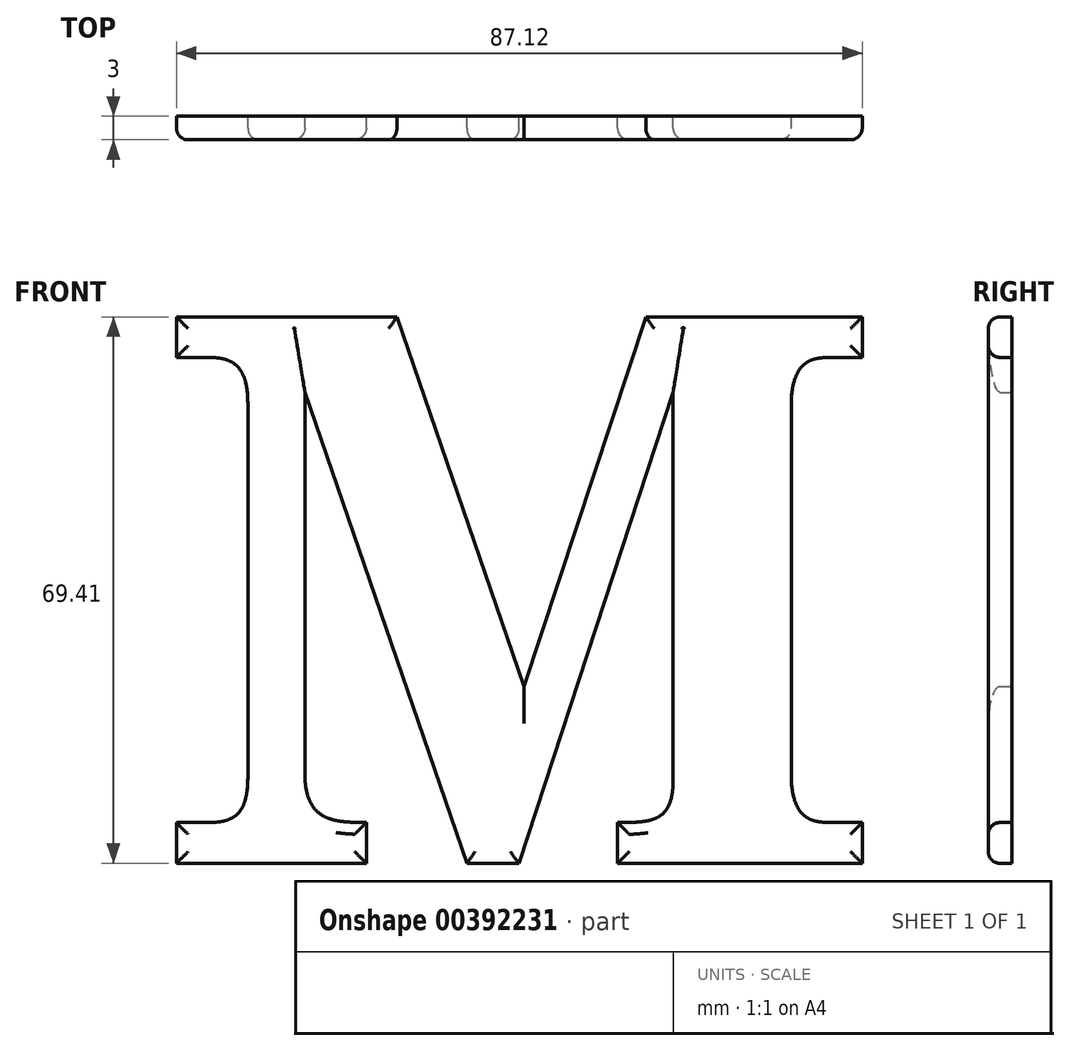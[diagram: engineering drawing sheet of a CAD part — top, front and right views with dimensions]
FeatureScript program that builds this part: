
annotation { "Feature Type Name" : "Feature", "Feature Type Description" : "" }
export const myFeature = defineFeature(function(context is Context, id is Id, definition is map)
    precondition{}
    {
        {
            var Q0;
            Q0=qCreatedBy(makeId("Front.planeOp"),FACE);
            var sketch = newSketch(context, id + "F0", { "sketchPlane" : qUnion([Q0])});
            skText(sketch, "E0", { "text": "M", "fontName": "NotoSerif-Bold.ttf"});
            const initialGuessF0  = {"E0": [0, 0, 1, 0, 0.07]};
            skSetInitialGuess(sketch, initialGuessF0);
            skSolve(sketch);
        }
        {
            var Q0;
            Q0 = qSketchRegion(id + "F0", true);
            extrude(context, id + "F1", {"entities" : qUnion([Q0]), "depth" : 3 * mm});
        }
        {
            var Q0;
            Q0=makeQuery(id+"F1.opExtrude","CAP_FACE",FACE,{"disambiguationData":[OSD([sQuery(id+"F0.wireOp",EDGE,"E0.sketch_text.stroke-0"),sQuery(id+"F0.wireOp",EDGE,"E0.sketch_text.stroke-1"),sQuery(id+"F0.wireOp",EDGE,"E0.sketch_text.stroke-2"),sQuery(id+"F0.wireOp",EDGE,"E0.sketch_text.stroke-3"),sQuery(id+"F0.wireOp",EDGE,"E0.sketch_text.stroke-4"),sQuery(id+"F0.wireOp",EDGE,"E0.sketch_text.stroke-5"),sQuery(id+"F0.wireOp",EDGE,"E0.sketch_text.stroke-6"),sQuery(id+"F0.wireOp",EDGE,"E0.sketch_text.stroke-7"),sQuery(id+"F0.wireOp",EDGE,"E0.sketch_text.stroke-8"),sQuery(id+"F0.wireOp",EDGE,"E0.sketch_text.stroke-9"),sQuery(id+"F0.wireOp",EDGE,"E0.sketch_text.stroke-10"),sQuery(id+"F0.wireOp",EDGE,"E0.sketch_text.stroke-11"),sQuery(id+"F0.wireOp",EDGE,"E0.sketch_text.stroke-12"),sQuery(id+"F0.wireOp",EDGE,"E0.sketch_text.stroke-13"),sQuery(id+"F0.wireOp",EDGE,"E0.sketch_text.stroke-14"),sQuery(id+"F0.wireOp",EDGE,"E0.sketch_text.stroke-15"),sQuery(id+"F0.wireOp",EDGE,"E0.sketch_text.stroke-16"),sQuery(id+"F0.wireOp",EDGE,"E0.sketch_text.stroke-17"),sQuery(id+"F0.wireOp",EDGE,"E0.sketch_text.stroke-18"),sQuery(id+"F0.wireOp",EDGE,"E0.sketch_text.stroke-19"),sQuery(id+"F0.wireOp",EDGE,"E0.sketch_text.stroke-20"),sQuery(id+"F0.wireOp",EDGE,"E0.sketch_text.stroke-21"),sQuery(id+"F0.wireOp",EDGE,"E0.sketch_text.stroke-22"),sQuery(id+"F0.wireOp",EDGE,"E0.sketch_text.stroke-23"),sQuery(id+"F0.wireOp",EDGE,"E0.sketch_text.stroke-24"),sQuery(id+"F0.wireOp",EDGE,"E0.sketch_text.stroke-25"),sQuery(id+"F0.wireOp",EDGE,"E0.sketch_text.stroke-26"),sQuery(id+"F0.wireOp",EDGE,"E0.sketch_text.stroke-27"),sQuery(id+"F0.wireOp",EDGE,"E0.sketch_text.stroke-28"),sQuery(id+"F0.wireOp",EDGE,"E0.sketch_text.stroke-29"),sQuery(id+"F0.wireOp",EDGE,"E0.sketch_text.stroke-30"),sQuery(id+"F0.wireOp",EDGE,"E0.sketch_text.stroke-31"),sQuery(id+"F0.wireOp",EDGE,"E0.sketch_text.stroke-32"),sQuery(id+"F0.wireOp",EDGE,"E0.sketch_text.stroke-33"),sQuery(id+"F0.wireOp",EDGE,"E0.sketch_text.stroke-34"),sQuery(id+"F0.wireOp",EDGE,"E0.sketch_text.stroke-35"),sQuery(id+"F0.wireOp",EDGE,"E0.sketch_text.stroke-36"),sQuery(id+"F0.wireOp",EDGE,"E0.sketch_text.stroke-37"),sQuery(id+"F0.wireOp",EDGE,"E0.sketch_text.stroke-38"),sQuery(id+"F0.wireOp",EDGE,"E0.sketch_text.stroke-39"),sQuery(id+"F0.wireOp",EDGE,"E0.sketch_text.stroke-40"),sQuery(id+"F0.wireOp",EDGE,"E0.sketch_text.stroke-41"),sQuery(id+"F0.wireOp",EDGE,"E0.sketch_text.stroke-42"),sQuery(id+"F0.wireOp",EDGE,"E0.sketch_text.stroke-43"),sQuery(id+"F0.wireOp",EDGE,"E0.sketch_text.stroke-44"),sQuery(id+"F0.wireOp",EDGE,"E0.sketch_text.stroke-45"),sQuery(id+"F0.wireOp",EDGE,"E0.sketch_text.stroke-46"),sQuery(id+"F0.wireOp",EDGE,"E0.sketch_text.stroke-47"),sQuery(id+"F0.wireOp",EDGE,"E0.sketch_text.stroke-48")])],"isStart":false});
            fillet(context, id + "F2", {"entities" : qUnion([Q0]), "radius" : 1.5 * mm, "tangentPropagation" : true, "allowEdgeOverflow" : false});
        }
    });
